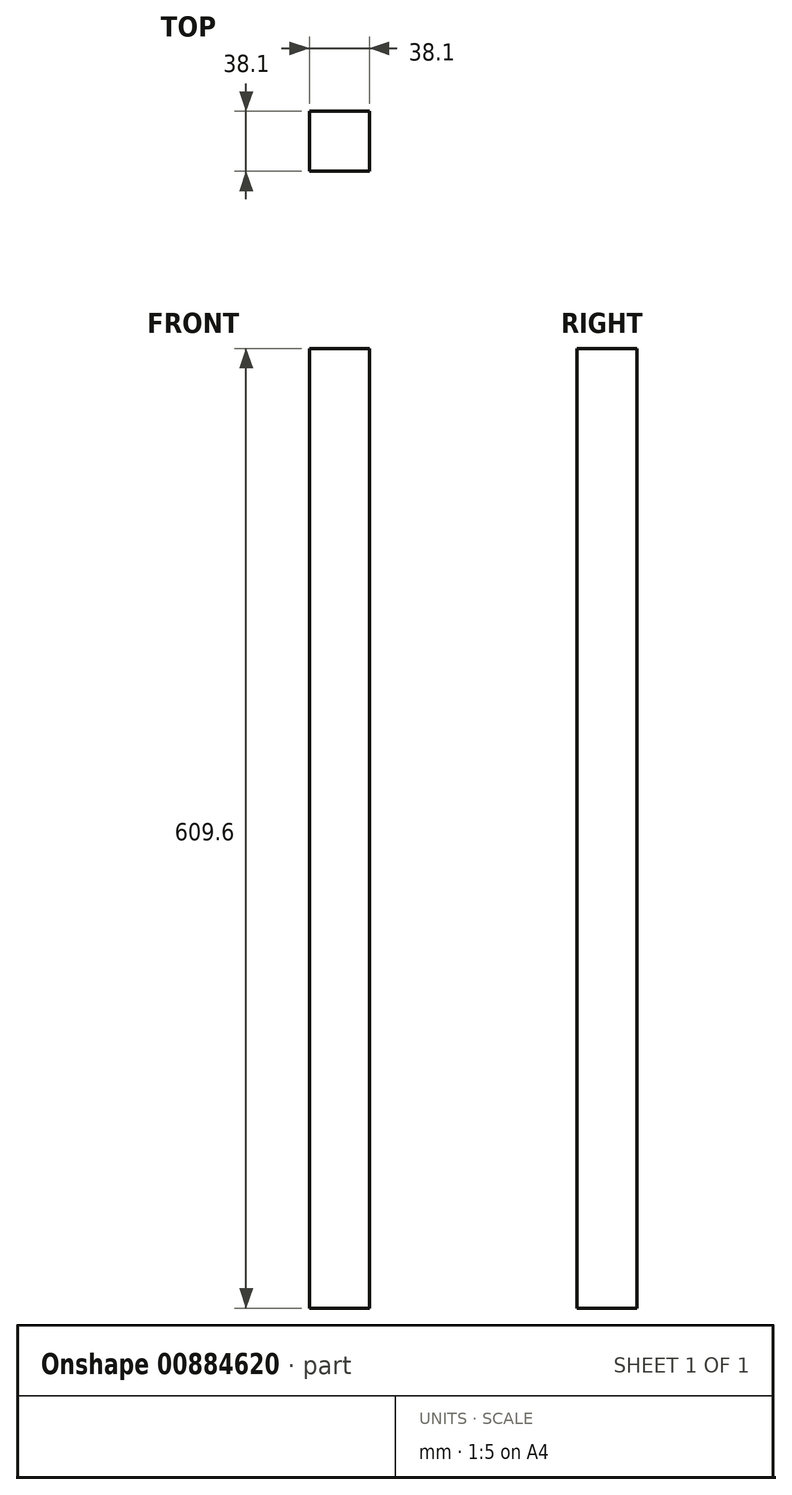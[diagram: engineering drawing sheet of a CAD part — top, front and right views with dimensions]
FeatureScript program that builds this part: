
annotation { "Feature Type Name" : "Feature", "Feature Type Description" : "" }
export const myFeature = defineFeature(function(context is Context, id is Id, definition is map)
    precondition{}
    {
        {
            var Q0;
            Q0=qCreatedBy(makeId("Front.planeOp"),FACE);
            var sketch = newSketch(context, id + "F0", { "sketchPlane" : qUnion([Q0])});
            skLineSegment(sketch, "E0.bottom", {"start": v(19.05, 304.8) * mm, "end": v(-19.05, 304.8) * mm});
            skLineSegment(sketch, "E0.top", {"start": v(19.05, -304.8) * mm, "end": v(-19.05, -304.8) * mm});
            skLineSegment(sketch, "E0.left", {"start": v(19.05, 304.8) * mm, "end": v(19.05, -304.8) * mm});
            skLineSegment(sketch, "E0.right", {"start": v(-19.05, 304.8) * mm, "end": v(-19.05, -304.8) * mm});
            skPoint(sketch, "E0.middle", {"position": v(0, 0) * mm});
            skSolve(sketch);
        }
        {
            var Q0;
            Q0 = qSketchRegion(id + "F0", true);
            extrude(context, id + "F1", {"entities" : qUnion([Q0]), "depth" : 38.1 * mm, "offsetDistance" : 25.4 * mm});
        }
    });
